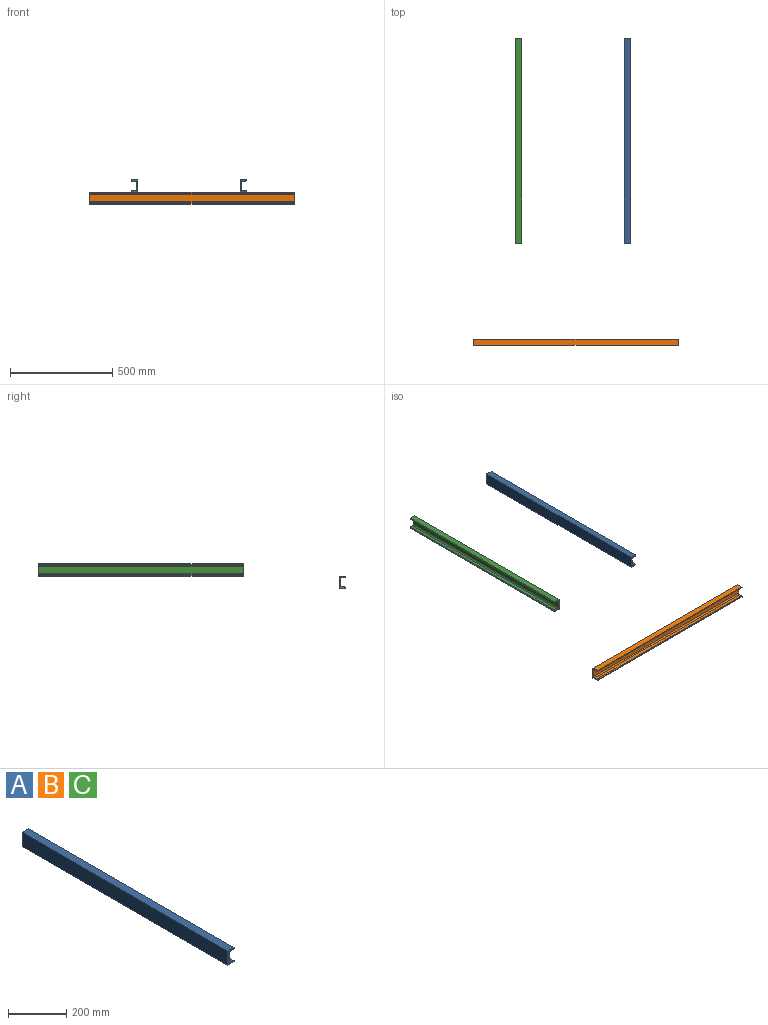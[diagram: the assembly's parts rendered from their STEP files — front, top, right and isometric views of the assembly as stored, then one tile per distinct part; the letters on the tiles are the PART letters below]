
ASSEMBLY  parts=3 mates=2
PART A: 14 faces, bbox 30x1000x60 mm
  f0: plane 1000x3.25mm, normal (1,0,0), area 3250mm2, adj f1,f11,f12,f13
  f1: plane 1000x30mm, normal (0,0,1), area 30000mm2, adj f0,f2,f12,f13
  f2: plane 1000x60mm, normal (-1,0,0), area 60000mm2, adj f1,f3,f12,f13
  f3: plane 1000x30mm, normal (0,0,-1), area 30000mm2, adj f2,f4,f12,f13
  f4: plane 1000x3.25mm, normal (1,0,0), area 3250mm2, adj f3,f5,f12,f13
  f5: cylinder r=3mm len=1000mm, axis (0,1,0), area 4712.4mm2, adj f4,f6,f12,f13
  f6: plane 1000x15mm, normal (0,0,1), area 15000mm2, adj f5,f7,f12,f13
  f7: cylinder r=6mm len=1000mm, axis (0,1,0), area 9424.8mm2, adj f6,f8,f12,f13
  f8: plane 1000x35.5mm, normal (1,0,0), area 35500mm2, adj f7,f9,f12,f13
  f9: cylinder r=6mm len=1000mm, axis (0,1,0), area 9424.8mm2, adj f8,f10,f12,f13
  f10: plane 1000x15mm, normal (0,0,-1), area 15000mm2, adj f9,f11,f12,f13
  f11: cylinder r=3mm len=1000mm, axis (0,1,0), area 4712.4mm2, adj f0,f10,f12,f13
  f12: plane 60x30mm, normal (0,-1,0), area 671.6mm2, adj f0,f1,f2,f3,f4,f5,f6,f7
  f13: plane 60x30mm, normal (0,1,0), area 671.6mm2, adj f0,f1,f2,f3,f4,f5,f6,f7
PART B: same geometry as A
PART C: same geometry as A
PLACE A t=(-61.72,-38.37,-47.09)mm fixed
PLACE B rot(axis=(0,0,-1),90deg) t=(-296.72,-1008.37,-107.09)mm
PLACE C rot(axis=(0,1,0),180deg) t=(-561.72,-38.37,12.49)mm fixed
MATE planar B.f1 <-> A.f3  axis (0,0,1) through (-296.72,-1023.37,-47.09)mm
MATE parallel C.f2 <-> A.f2  axis (1,0,0) through (-561.72,-38.37,-17.51)mm
